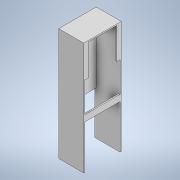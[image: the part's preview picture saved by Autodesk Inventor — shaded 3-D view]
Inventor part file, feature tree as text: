
AUTODESK INVENTOR PART (.ipt)
format: ipt  version: 2020 (Build 240168000, 168)  size: 144,896 bytes
history: native  units: mm
features: extrude x5, sketch x5, mirror x1
ambient origin geometry x8: Origin, YZ Plane, XZ Plane, XY Plane, X Axis, Y Axis, Z Axis, Center Point
bodies: Solid1 (feature_tree)
feature tree (11):
  extrude  "Extrusion1"  Depth=60.0mm
  extrude  "Extrusion2"  Depth=38.0mm
  extrude  "Extrusion3"  Depth=2.0mm TaperAngle=0.0deg
  mirror  "Mirror1"
  extrude  "Extrusion4"  Depth=50.0mm
  extrude  "Extrusion5"  Depth=70.0mm
  sketch  "Sketch1"  dims[d0=40.0mm d1=60.0mm]
  sketch  "Sketch2"  dims[d2=2.0mm d3=38.0mm]
  sketch  "Sketch3"  dims[d4=180.0mm d5=0.0mm d6=2.0mm d7=0.0mm]
  sketch  "Sketch4"  dims[d8=2.0mm d9=50.0mm]
  sketch  "Sketch5"  dims[d10=5.0mm d11=0.0mm d12=70.0mm d13=5.0mm d14=0.0mm d15=10.0mm d16=2.0mm d17=0.0mm]
